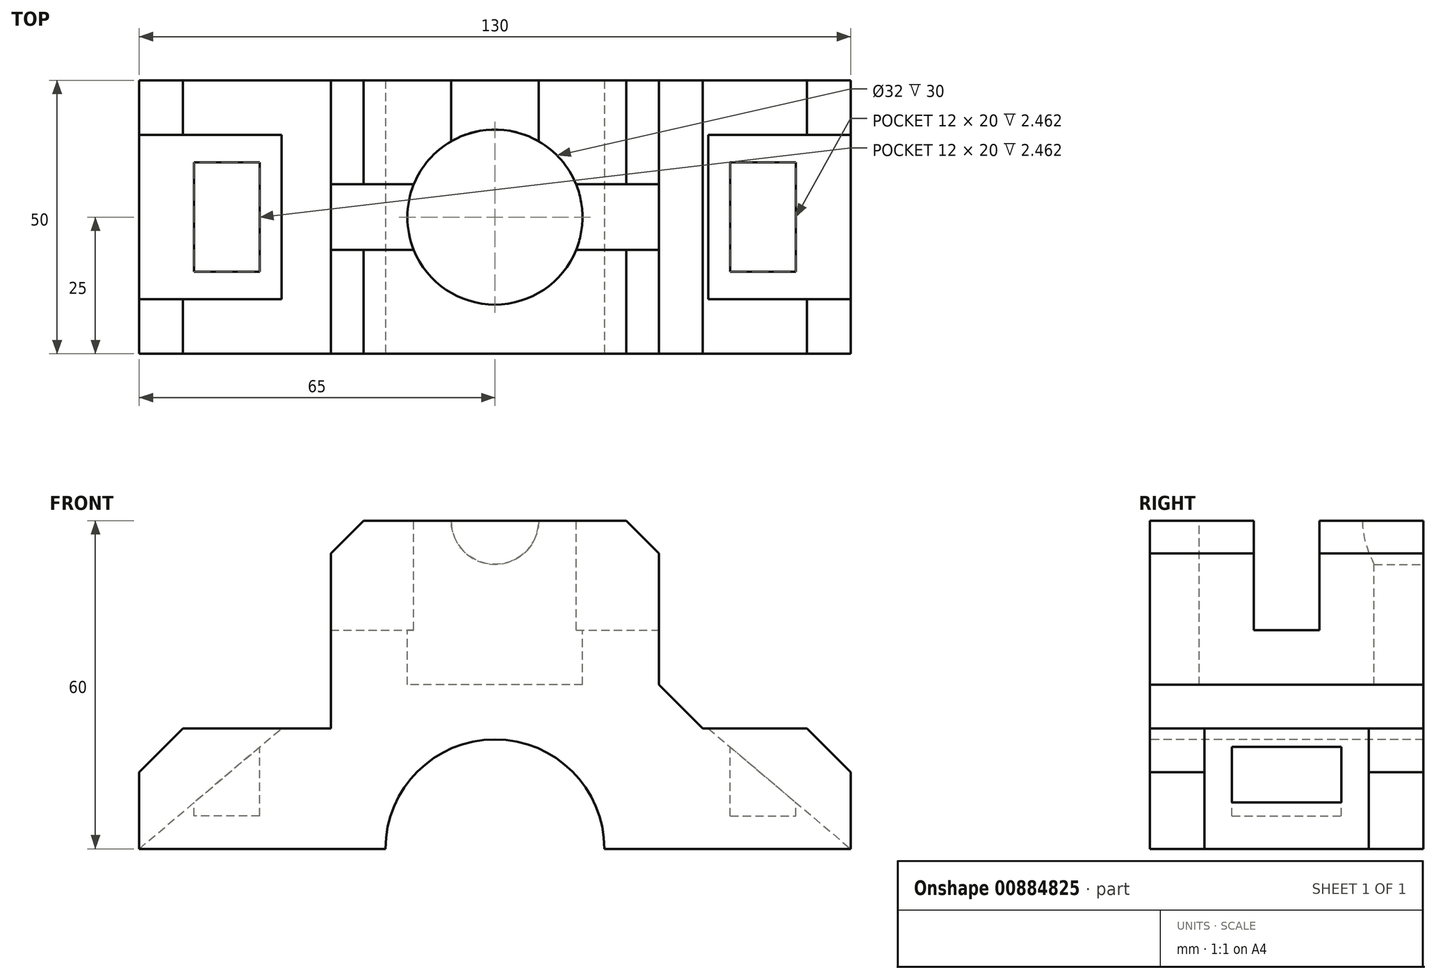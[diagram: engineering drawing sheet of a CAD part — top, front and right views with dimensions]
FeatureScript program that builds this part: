
annotation { "Feature Type Name" : "Feature", "Feature Type Description" : "" }
export const myFeature = defineFeature(function(context is Context, id is Id, definition is map)
    precondition{}
    {
        {
            var Q0;
            Q0=qCreatedBy(makeId("Front.planeOp"),FACE);
            var sketch = newSketch(context, id + "F0", { "sketchPlane" : qUnion([Q0])});
            skLineSegment(sketch, "E0.bottom", {"start": v(-65, -30) * mm, "end": v(65, -30) * mm});
            skLineSegment(sketch, "E0.top", {"start": v(-30, 30) * mm, "end": v(30, 30) * mm});
            skLineSegment(sketch, "E0.left", {"start": v(-65, -30) * mm, "end": v(-65, -8) * mm});
            skLineSegment(sketch, "E0.right", {"start": v(65, -30) * mm, "end": v(65, -8) * mm});
            skPoint(sketch, "E0.middle", {"position": v(0, 0) * mm});
            skLineSegment(sketch, "E1", {"start": v(-65, -8) * mm, "end": v(-30, -8) * mm});
            skLineSegment(sketch, "E2", {"start": v(-30, -8) * mm, "end": v(-30, 30) * mm});
            skLineSegment(sketch, "E3", {"start": v(30, 30) * mm, "end": v(30, -8) * mm});
            skLineSegment(sketch, "E4", {"start": v(30, -8) * mm, "end": v(65, -8) * mm});
            skLineSegment(sketch, "E5", {"start": v(65, -8) * mm, "end": v(65, -30) * mm});
            skPoint(sketch, "E6.orphan", {"position": v(-65, 30) * mm});
            skPoint(sketch, "E7.orphan", {"position": v(65, 30) * mm});
            skSolve(sketch);
        }
        {
            var Q0;
            Q0 = qSketchRegion(id + "F0", true);
            extrude(context, id + "F1", {"entities" : qUnion([Q0]), "depth" : 50 * mm, "offsetDistance" : 25.4 * mm});
        }
        {
            var Q0;
            Q0=makeQuery(id+"F1.opExtrude","SWEPT_EDGE",EDGE,{"disambiguationData":[OSD([sQuery(id+"F0.wireOp",EDGE,"E0.left"),sQuery(id+"F0.wireOp",EDGE,"E1")])]});
            var Q1;
            Q1=makeQuery(id+"F1.opExtrude","SWEPT_EDGE",EDGE,{"disambiguationData":[OSD([sQuery(id+"F0.wireOp",EDGE,"E4"),sQuery(id+"F0.wireOp",EDGE,"E5")])]});
            chamfer(context, id + "F2", {"entities" : qUnion([Q0, Q1]), "width" : 8 * mm, "tangentPropagation" : true});
        }
        {
            var Q0;
            Q0=makeQuery(id+"F1.opExtrude","SWEPT_EDGE",EDGE,{"disambiguationData":[OSD([sQuery(id+"F0.wireOp",EDGE,"E2"),sQuery(id+"F0.wireOp",EDGE,"E0.top")])]});
            var Q1;
            Q1=makeQuery(id+"F1.opExtrude","SWEPT_EDGE",EDGE,{"disambiguationData":[OSD([sQuery(id+"F0.wireOp",EDGE,"E0.top"),sQuery(id+"F0.wireOp",EDGE,"E3")])]});
            chamfer(context, id + "F3", {"entities" : qUnion([Q0, Q1]), "width" : 6 * mm, "tangentPropagation" : true});
        }
        {
            var Q0;
            Q0=makeQuery(id+"F1.opExtrude","SWEPT_FACE",FACE,{"disambiguationData":[OSD([sQuery(id+"F0.wireOp",EDGE,"E0.top")])]});
            var sketch = newSketch(context, id + "F4", { "sketchPlane" : qUnion([Q0])});
            skLineSegment(sketch, "E8.bottom", {"start": v(-30, -31) * mm, "end": v(30, -31) * mm});
            skLineSegment(sketch, "E8.top", {"start": v(-30, -19) * mm, "end": v(30, -19) * mm});
            skLineSegment(sketch, "E8.left", {"start": v(-30, -31) * mm, "end": v(-30, -19) * mm});
            skLineSegment(sketch, "E8.right", {"start": v(30, -31) * mm, "end": v(30, -19) * mm});
            skPoint(sketch, "E8.middle", {"position": v(0, -25) * mm});
            skPoint(sketch, "E8.middle.positionSnap0", {"position": v(-24, -25) * mm});
            skPoint(sketch, "E8.centerSnap0", {"position": v(-24, -25) * mm});
            skCircle(sketch, "E9", {"center": v(0, -25) * mm, "radius": 16 * mm});
            skSolve(sketch);
        }
        {
            var Q0;
            {var subQ0=sQuery(id+"F4.wireOp",EDGE,"E8.left");Q0=makeQuery(id+"F4.imprint","IMPRINT",FACE,{"disambiguationData":[TD([[makeQuery(id+"F4.imprint","IMPRINT",EDGE,{"derivedFrom":subQ0}),-1.0]])]});}
            var Q1;
            {var subQ0=sQuery(id+"F4.wireOp",EDGE,"E8.right");Q1=makeQuery(id+"F4.imprint","IMPRINT",FACE,{"disambiguationData":[TD([[makeQuery(id+"F4.imprint","IMPRINT",EDGE,{"derivedFrom":subQ0}),1.0]])]});}
            var Q2;
            {var subQ0=sQuery(id+"F4.wireOp",EDGE,"E9");var subQ1=sQuery(id+"F4.wireOp",EDGE,"E8.bottom");var subQ2=makeQuery(id+"F4.imprint","INTERSECT",VERTEX,{"disambiguationData":[OD(0.0)],"derivedFrom":[subQ1,subQ0]});Q2=makeQuery(id+"F4.imprint","IMPRINT",FACE,{"disambiguationData":[TD([[makeQuery(id+"F4.imprint","IMPRINT",EDGE,{"disambiguationData":[TD([[subQ2,1.0]])],"derivedFrom":subQ0}),-1.0]])]});}
            var Q3;
            {var subQ0=sQuery(id+"F4.wireOp",EDGE,"E9");var subQ1=sQuery(id+"F4.wireOp",EDGE,"E8.bottom");var subQ2=makeQuery(id+"F4.imprint","INTERSECT",VERTEX,{"disambiguationData":[OD(1.0)],"derivedFrom":[subQ1,subQ0]});Q3=makeQuery(id+"F4.imprint","IMPRINT",FACE,{"disambiguationData":[TD([[makeQuery(id+"F4.imprint","IMPRINT",EDGE,{"disambiguationData":[TD([[subQ2,-1.0]])],"derivedFrom":subQ0}),-1.0]])]});}
            extrude(context, id + "F5", {"entities" : qUnion([Q0, Q1, Q2, Q3]), "operationType" : NewBodyOperationType.REMOVE, "oppositeDirection" : true, "depth" : 20 * mm, "offsetDistance" : 25.4 * mm});
        }
        {
            var Q0;
            Q0=makeQuery(id+"F1.opExtrude","SWEPT_FACE",FACE,{"disambiguationData":[OSD([sQuery(id+"F0.wireOp",EDGE,"E0.top")])]});
            var sketch = newSketch(context, id + "F6", { "sketchPlane" : qUnion([Q0])});
            skCircle(sketch, "E10", {"center": v(0, -25) * mm, "radius": 16 * mm});
            skSolve(sketch);
        }
        {
            var Q0;
            Q0 = qSketchRegion(id + "F6", true);
            extrude(context, id + "F7", {"entities" : qUnion([Q0]), "operationType" : NewBodyOperationType.REMOVE, "oppositeDirection" : true, "depth" : 30 * mm, "offsetDistance" : 25.4 * mm});
        }
        {
            var Q0;
            Q0=makeQuery(id+"F1.opExtrude","CAP_FACE",FACE,{"disambiguationData":[OSD([sQuery(id+"F0.wireOp",EDGE,"E0.bottom"),sQuery(id+"F0.wireOp",EDGE,"E0.left"),sQuery(id+"F0.wireOp",EDGE,"E1"),sQuery(id+"F0.wireOp",EDGE,"E2"),sQuery(id+"F0.wireOp",EDGE,"E0.top"),sQuery(id+"F0.wireOp",EDGE,"E3"),sQuery(id+"F0.wireOp",EDGE,"E4"),sQuery(id+"F0.wireOp",EDGE,"E5")])],"isStart":true});
            var sketch = newSketch(context, id + "F8", { "sketchPlane" : qUnion([Q0])});
            skCircle(sketch, "E11", {"center": v(0, 30) * mm, "radius": 8 * mm});
            skSolve(sketch);
        }
        {
            var Q0;
            Q0 = qSketchRegion(id + "F8", true);
            extrude(context, id + "F9", {"entities" : qUnion([Q0]), "operationType" : NewBodyOperationType.REMOVE, "oppositeDirection" : true, "depth" : 25.4 * mm, "offsetDistance" : 25.4 * mm});
        }
        {
            var Q0;
            Q0=makeQuery(id+"F1.opExtrude","SWEPT_FACE",FACE,{"disambiguationData":[OSD([sQuery(id+"F0.wireOp",EDGE,"E1")])]});
            var sketch = newSketch(context, id + "F10", { "sketchPlane" : qUnion([Q0])});
            skLineSegment(sketch, "E12", {"start": v(-30, -50) * mm, "end": v(-39, -50) * mm});
            skLineSegment(sketch, "E13", {"start": v(-39, -50) * mm, "end": v(-39, -40) * mm});
            skLineSegment(sketch, "E14", {"start": v(-39, -40) * mm, "end": v(-39, -10) * mm});
            skLineSegment(sketch, "E15", {"start": v(-39, -10) * mm, "end": v(-39, 0) * mm});
            skLineSegment(sketch, "E16.bottom", {"start": v(-39, -10) * mm, "end": v(-149.05, -10) * mm});
            skLineSegment(sketch, "E16.top", {"start": v(-39, -40) * mm, "end": v(-149.05, -40) * mm});
            skLineSegment(sketch, "E16.left", {"start": v(-39, -10) * mm, "end": v(-39, -40) * mm});
            skLineSegment(sketch, "E16.right", {"start": v(-149.05, -10) * mm, "end": v(-149.05, -40) * mm});
            skSolve(sketch);
        }
        {
            var Q0;
            Q0 = qSketchRegion(id + "F10", true);
            extrude(context, id + "F11", {"entities" : qUnion([Q0]), "operationType" : NewBodyOperationType.REMOVE, "endBound" : BoundingType.THROUGH_ALL, "oppositeDirection" : true, "depth" : 18 * mm, "offsetDistance" : 25.4 * mm});
        }
        {
            var Q0;
            Q0=makeQuery(id+"F1.opExtrude","SWEPT_FACE",FACE,{"disambiguationData":[OSD([sQuery(id+"F0.wireOp",EDGE,"E4")])]});
            var sketch = newSketch(context, id + "F12", { "sketchPlane" : qUnion([Q0])});
            skLineSegment(sketch, "E17", {"start": v(30, -50) * mm, "end": v(39, -50) * mm});
            skLineSegment(sketch, "E18", {"start": v(39, -50) * mm, "end": v(39, -40) * mm});
            skLineSegment(sketch, "E19", {"start": v(39, -40) * mm, "end": v(39, -10) * mm});
            skLineSegment(sketch, "E20", {"start": v(39, -10) * mm, "end": v(39, 0) * mm});
            skLineSegment(sketch, "E21.bottom", {"start": v(39, -40) * mm, "end": v(151.45, -40) * mm});
            skLineSegment(sketch, "E21.top", {"start": v(39, -10) * mm, "end": v(151.45, -10) * mm});
            skLineSegment(sketch, "E21.right", {"start": v(151.45, -40) * mm, "end": v(151.45, -10) * mm});
            skSolve(sketch);
        }
        {
            var Q0;
            Q0 = qSketchRegion(id + "F12", true);
            extrude(context, id + "F13", {"entities" : qUnion([Q0]), "operationType" : NewBodyOperationType.REMOVE, "endBound" : BoundingType.THROUGH_ALL, "oppositeDirection" : true, "depth" : 25.4 * mm, "offsetDistance" : 25.4 * mm});
        }
        {
            var Q0;
            Q0=makeQuery(id+"F13.boolean.opBoolean","COPY",FACE,{"derivedFrom":makeQuery(id+"F13.opExtrude","SWEPT_FACE",FACE,{"disambiguationData":[OSD([sQuery(id+"F12.wireOp",EDGE,"E21.top")])]})});
            var sketch = newSketch(context, id + "F14", { "sketchPlane" : qUnion([Q0])});
            skLineSegment(sketch, "E22", {"start": v(65, -30) * mm, "end": v(39, -30) * mm});
            skLineSegment(sketch, "E23", {"start": v(39, -30) * mm, "end": v(39, -8) * mm});
            skLineSegment(sketch, "E24", {"start": v(39, -8) * mm, "end": v(65, -30) * mm});
            skSolve(sketch);
        }
        {
            var Q0;
            Q0 = qSketchRegion(id + "F14", true);
            extrude(context, id + "F15", {"entities" : qUnion([Q0]), "operationType" : NewBodyOperationType.ADD, "depth" : 30 * mm, "offsetDistance" : 25.4 * mm});
        }
        {
            var Q0;
            Q0=makeQuery(id+"F11.boolean.opBoolean","COPY",FACE,{"derivedFrom":makeQuery(id+"F11.opExtrude","SWEPT_FACE",FACE,{"disambiguationData":[OSD([sQuery(id+"F10.wireOp",EDGE,"E16.bottom")])]})});
            var sketch = newSketch(context, id + "F16", { "sketchPlane" : qUnion([Q0])});
            skLineSegment(sketch, "E25", {"start": v(-39, -30) * mm, "end": v(-65, -30) * mm});
            skLineSegment(sketch, "E26", {"start": v(-65, -30) * mm, "end": v(-39, -8) * mm});
            skSolve(sketch);
        }
        {
            var Q0;
            Q0=makeQuery(id+"F16.imprint","IMPRINT",FACE,{"disambiguationData":[TD([[makeQuery(id+"F16.imprint","IMPRINT",EDGE,{"derivedFrom":sQuery(id+"F16.wireOp",EDGE,"E25")}),-1.0]])]});
            extrude(context, id + "F17", {"entities" : qUnion([Q0]), "operationType" : NewBodyOperationType.ADD, "depth" : 30 * mm, "offsetDistance" : 25.4 * mm});
        }
        {
            var Q0;
            Q0=makeQuery(id+"F1.opExtrude","SWEPT_FACE",FACE,{"disambiguationData":[OSD([sQuery(id+"F0.wireOp",EDGE,"E4")])]});
            var sketch = newSketch(context, id + "F18", { "sketchPlane" : qUnion([Q0])});
            skLineSegment(sketch, "E27", {"start": v(39, -40) * mm, "end": v(39, -35) * mm});
            skLineSegment(sketch, "E28", {"start": v(39, -35) * mm, "end": v(39, -15) * mm});
            skLineSegment(sketch, "E29", {"start": v(39, -15) * mm, "end": v(39, -10) * mm});
            skLineSegment(sketch, "E30", {"start": v(39, -35) * mm, "end": v(43, -35) * mm});
            skLineSegment(sketch, "E31", {"start": v(43, -35) * mm, "end": v(43, -15) * mm});
            skLineSegment(sketch, "E32", {"start": v(43, -15) * mm, "end": v(39, -15) * mm});
            skLineSegment(sketch, "E33.bottom", {"start": v(43, -35) * mm, "end": v(55, -35) * mm});
            skLineSegment(sketch, "E33.top", {"start": v(43, -15) * mm, "end": v(55, -15) * mm});
            skLineSegment(sketch, "E33.right", {"start": v(55, -35) * mm, "end": v(55, -15) * mm});
            skSolve(sketch);
        }
        {
            var Q0;
            Q0=makeQuery(id+"F18.imprint","IMPRINT",FACE,{"disambiguationData":[TD([[makeQuery(id+"F18.imprint","IMPRINT",EDGE,{"derivedFrom":sQuery(id+"F18.wireOp",EDGE,"E33.bottom")}),1.0]])]});
            extrude(context, id + "F19", {"entities" : qUnion([Q0]), "operationType" : NewBodyOperationType.REMOVE, "oppositeDirection" : true, "depth" : 16 * mm, "offsetDistance" : 25.4 * mm});
        }
        {
            var Q0;
            Q0=makeQuery(id+"F1.opExtrude","SWEPT_FACE",FACE,{"disambiguationData":[OSD([sQuery(id+"F0.wireOp",EDGE,"E1")])]});
            var sketch = newSketch(context, id + "F20", { "sketchPlane" : qUnion([Q0])});
            skLineSegment(sketch, "E34", {"start": v(-39, -40) * mm, "end": v(-39, -35) * mm});
            skLineSegment(sketch, "E35", {"start": v(-39, -35) * mm, "end": v(-39, -15) * mm});
            skLineSegment(sketch, "E36", {"start": v(-39, -15) * mm, "end": v(-39, -10) * mm});
            skLineSegment(sketch, "E37.bottom", {"start": v(-39, -35) * mm, "end": v(-43, -35) * mm});
            skLineSegment(sketch, "E37.top", {"start": v(-39, -15) * mm, "end": v(-43, -15) * mm});
            skLineSegment(sketch, "E37.right", {"start": v(-43, -35) * mm, "end": v(-43, -15) * mm});
            skLineSegment(sketch, "E38.bottom", {"start": v(-43, -35) * mm, "end": v(-55, -35) * mm});
            skLineSegment(sketch, "E38.top", {"start": v(-43, -15) * mm, "end": v(-55, -15) * mm});
            skLineSegment(sketch, "E38.right", {"start": v(-55, -35) * mm, "end": v(-55, -15) * mm});
            skSolve(sketch);
        }
        {
            var Q0;
            Q0=makeQuery(id+"F20.imprint","IMPRINT",FACE,{"disambiguationData":[TD([[makeQuery(id+"F20.imprint","IMPRINT",EDGE,{"derivedFrom":sQuery(id+"F20.wireOp",EDGE,"E38.bottom")}),-1.0]])]});
            extrude(context, id + "F21", {"entities" : qUnion([Q0]), "operationType" : NewBodyOperationType.REMOVE, "oppositeDirection" : true, "depth" : 16 * mm, "offsetDistance" : 25.4 * mm});
        }
        {
            var Q0;
            Q0=makeQuery(id+"F1.opExtrude","CAP_FACE",FACE,{"disambiguationData":[OSD([sQuery(id+"F0.wireOp",EDGE,"E0.bottom"),sQuery(id+"F0.wireOp",EDGE,"E0.left"),sQuery(id+"F0.wireOp",EDGE,"E1"),sQuery(id+"F0.wireOp",EDGE,"E2"),sQuery(id+"F0.wireOp",EDGE,"E0.top"),sQuery(id+"F0.wireOp",EDGE,"E3"),sQuery(id+"F0.wireOp",EDGE,"E4"),sQuery(id+"F0.wireOp",EDGE,"E5")])],"isStart":false});
            var sketch = newSketch(context, id + "F22", { "sketchPlane" : qUnion([Q0])});
            skCircle(sketch, "E39", {"center": v(0, -30) * mm, "radius": 20 * mm});
            skSolve(sketch);
        }
        {
            var Q0;
            Q0 = qSketchRegion(id + "F22", true);
            extrude(context, id + "F23", {"entities" : qUnion([Q0]), "operationType" : NewBodyOperationType.REMOVE, "endBound" : BoundingType.THROUGH_ALL, "oppositeDirection" : true, "depth" : 25.4 * mm, "offsetDistance" : 25.4 * mm});
        }
    });
